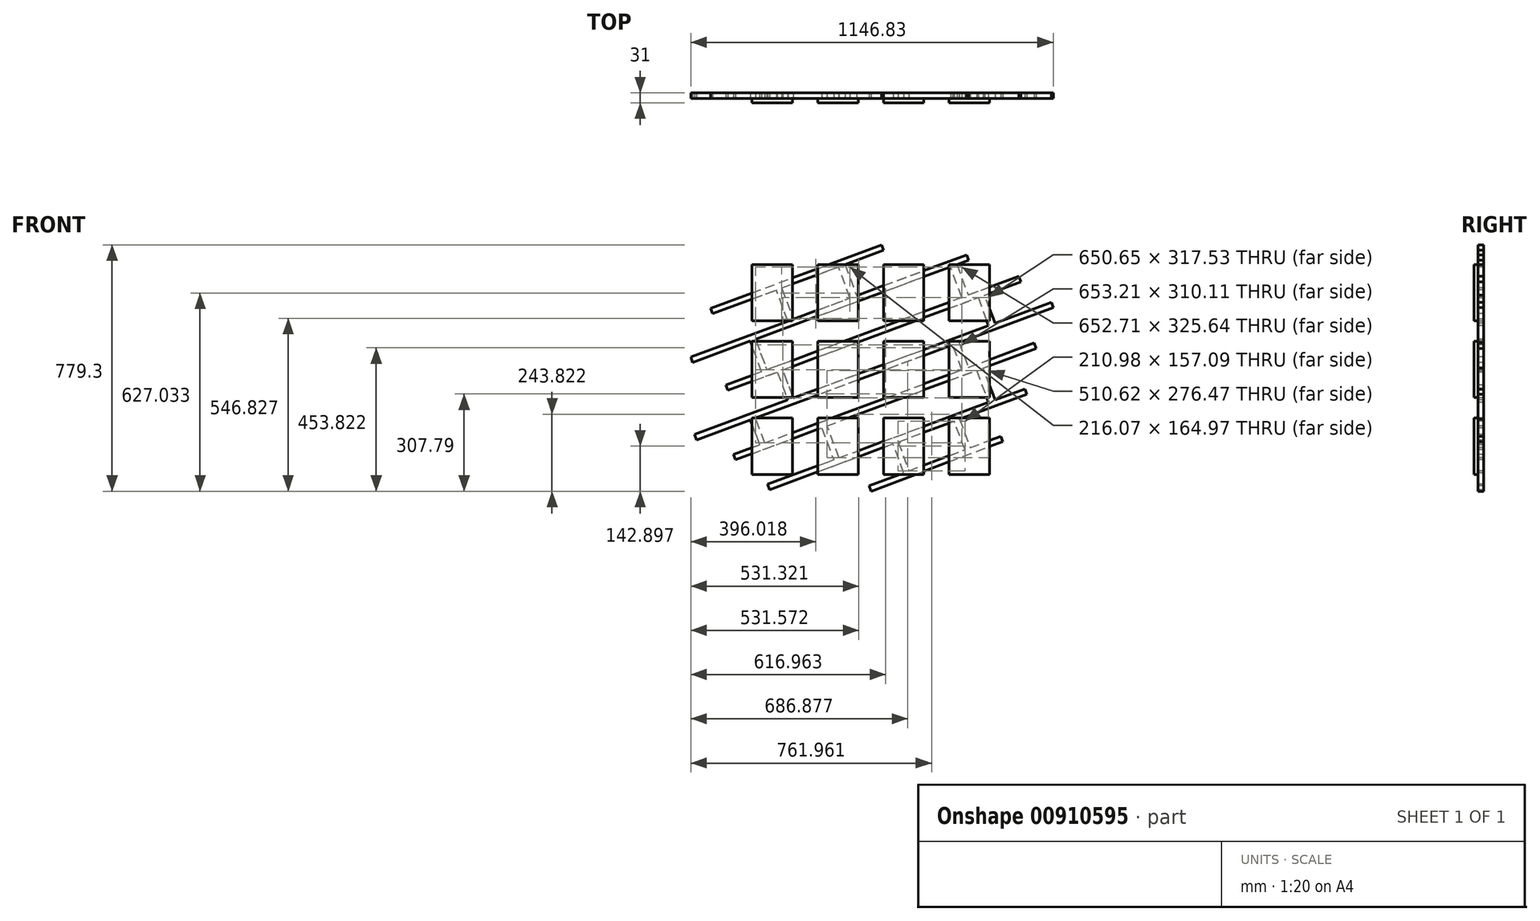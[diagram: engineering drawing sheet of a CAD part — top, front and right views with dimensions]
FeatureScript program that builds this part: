
annotation { "Feature Type Name" : "Feature", "Feature Type Description" : "" }
export const myFeature = defineFeature(function(context is Context, id is Id, definition is map)
    precondition{}
    {
        {
            var Q0;
            Q0=qCreatedBy(makeId("Front.planeOp"),FACE);
            var sketch = newSketch(context, id + "F0", { "sketchPlane" : qUnion([Q0])});
            skLineSegment(sketch, "E0.bottom", {"start": v(-52.91, 29.92) * mm, "end": v(75.09, 29.92) * mm});
            skLineSegment(sketch, "E0.top", {"start": v(-52.91, -148.08) * mm, "end": v(75.09, -148.08) * mm});
            skLineSegment(sketch, "E0.left", {"start": v(-52.91, 29.92) * mm, "end": v(-52.91, -148.08) * mm});
            skLineSegment(sketch, "E0.right", {"start": v(75.09, 29.92) * mm, "end": v(75.09, -148.08) * mm});
            skLineSegment(sketch, "E1.bottom", {"start": v(155.09, 29.92) * mm, "end": v(283.09, 29.92) * mm});
            skLineSegment(sketch, "E1.top", {"start": v(155.09, -148.08) * mm, "end": v(283.09, -148.08) * mm});
            skLineSegment(sketch, "E1.left", {"start": v(155.09, 29.92) * mm, "end": v(155.09, -148.08) * mm});
            skLineSegment(sketch, "E1.right", {"start": v(283.09, 29.92) * mm, "end": v(283.09, -148.08) * mm});
            skLineSegment(sketch, "E2.bottom", {"start": v(363.09, 29.92) * mm, "end": v(491.09, 29.92) * mm});
            skLineSegment(sketch, "E2.top", {"start": v(363.09, -148.08) * mm, "end": v(491.09, -148.08) * mm});
            skLineSegment(sketch, "E2.left", {"start": v(363.09, 29.92) * mm, "end": v(363.09, -148.08) * mm});
            skLineSegment(sketch, "E2.right", {"start": v(491.09, 29.92) * mm, "end": v(491.09, -148.08) * mm});
            skLineSegment(sketch, "E3.bottom", {"start": v(571.09, 29.92) * mm, "end": v(699.09, 29.92) * mm});
            skLineSegment(sketch, "E3.top", {"start": v(571.09, -148.08) * mm, "end": v(699.09, -148.08) * mm});
            skLineSegment(sketch, "E3.left", {"start": v(571.09, 29.92) * mm, "end": v(571.09, -148.08) * mm});
            skLineSegment(sketch, "E3.right", {"start": v(699.09, 29.92) * mm, "end": v(699.09, -148.08) * mm});
            skLineSegment(sketch, "E4.bottom", {"start": v(-52.91, -213.08) * mm, "end": v(75.09, -213.08) * mm});
            skLineSegment(sketch, "E4.top", {"start": v(-52.91, -391.08) * mm, "end": v(75.09, -391.08) * mm});
            skLineSegment(sketch, "E4.left", {"start": v(-52.91, -213.08) * mm, "end": v(-52.91, -391.08) * mm});
            skLineSegment(sketch, "E4.right", {"start": v(75.09, -213.08) * mm, "end": v(75.09, -391.08) * mm});
            skLineSegment(sketch, "E5.bottom", {"start": v(155.09, -213.08) * mm, "end": v(283.09, -213.08) * mm});
            skLineSegment(sketch, "E5.top", {"start": v(155.09, -391.08) * mm, "end": v(283.09, -391.08) * mm});
            skLineSegment(sketch, "E5.left", {"start": v(155.09, -213.08) * mm, "end": v(155.09, -391.08) * mm});
            skLineSegment(sketch, "E5.right", {"start": v(283.09, -213.08) * mm, "end": v(283.09, -391.08) * mm});
            skLineSegment(sketch, "E6.bottom", {"start": v(363.09, -213.08) * mm, "end": v(491.09, -213.08) * mm});
            skLineSegment(sketch, "E6.top", {"start": v(363.09, -391.08) * mm, "end": v(491.09, -391.08) * mm});
            skLineSegment(sketch, "E6.left", {"start": v(363.09, -213.08) * mm, "end": v(363.09, -391.08) * mm});
            skLineSegment(sketch, "E6.right", {"start": v(491.09, -213.08) * mm, "end": v(491.09, -391.08) * mm});
            skLineSegment(sketch, "E7.bottom", {"start": v(571.09, -213.08) * mm, "end": v(699.09, -213.08) * mm});
            skLineSegment(sketch, "E7.top", {"start": v(571.09, -391.08) * mm, "end": v(699.09, -391.08) * mm});
            skLineSegment(sketch, "E7.left", {"start": v(571.09, -213.08) * mm, "end": v(571.09, -391.08) * mm});
            skLineSegment(sketch, "E7.right", {"start": v(699.09, -213.08) * mm, "end": v(699.09, -391.08) * mm});
            skLineSegment(sketch, "E8.bottom", {"start": v(-52.91, -456.08) * mm, "end": v(75.09, -456.08) * mm});
            skLineSegment(sketch, "E8.top", {"start": v(-52.91, -634.08) * mm, "end": v(75.09, -634.08) * mm});
            skLineSegment(sketch, "E8.left", {"start": v(-52.91, -456.08) * mm, "end": v(-52.91, -634.08) * mm});
            skLineSegment(sketch, "E8.right", {"start": v(75.09, -456.08) * mm, "end": v(75.09, -634.08) * mm});
            skLineSegment(sketch, "E9.bottom", {"start": v(155.09, -456.08) * mm, "end": v(283.09, -456.08) * mm});
            skLineSegment(sketch, "E9.top", {"start": v(155.09, -634.08) * mm, "end": v(283.09, -634.08) * mm});
            skLineSegment(sketch, "E9.left", {"start": v(155.09, -456.08) * mm, "end": v(155.09, -634.08) * mm});
            skLineSegment(sketch, "E9.right", {"start": v(283.09, -456.08) * mm, "end": v(283.09, -634.08) * mm});
            skLineSegment(sketch, "E10.bottom", {"start": v(363.09, -456.08) * mm, "end": v(491.09, -456.08) * mm});
            skLineSegment(sketch, "E10.top", {"start": v(363.09, -634.08) * mm, "end": v(491.09, -634.08) * mm});
            skLineSegment(sketch, "E10.left", {"start": v(363.09, -456.08) * mm, "end": v(363.09, -634.08) * mm});
            skLineSegment(sketch, "E10.right", {"start": v(491.09, -456.08) * mm, "end": v(491.09, -634.08) * mm});
            skLineSegment(sketch, "E11.bottom", {"start": v(571.09, -456.08) * mm, "end": v(699.09, -456.08) * mm});
            skLineSegment(sketch, "E11.top", {"start": v(571.09, -634.08) * mm, "end": v(699.09, -634.08) * mm});
            skLineSegment(sketch, "E11.left", {"start": v(571.09, -456.08) * mm, "end": v(571.09, -634.08) * mm});
            skLineSegment(sketch, "E11.right", {"start": v(699.09, -456.08) * mm, "end": v(699.09, -634.08) * mm});
            skLineSegment(sketch, "E12", {"start": v(75.09, 29.92) * mm, "end": v(155.09, 29.92) * mm, "construction": true});
            skLineSegment(sketch, "E13", {"start": v(283.09, 29.92) * mm, "end": v(363.09, 29.92) * mm, "construction": true});
            skLineSegment(sketch, "E14", {"start": v(491.09, 29.92) * mm, "end": v(571.09, 29.92) * mm, "construction": true});
            skLineSegment(sketch, "E15", {"start": v(-52.91, -148.08) * mm, "end": v(-52.91, -213.08) * mm, "construction": true});
            skLineSegment(sketch, "E16", {"start": v(-52.91, -391.08) * mm, "end": v(-52.91, -456.08) * mm, "construction": true});
            skSolve(sketch);
        }
        {
            var Q0;
            Q0=makeQuery(id+"F0.imprint","IMPRINT",FACE,{"disambiguationData":[TD([[makeQuery(id+"F0.imprint","IMPRINT",EDGE,{"derivedFrom":sQuery(id+"F0.wireOp",EDGE,"E1.bottom")}),-1.0]])]});
            var Q1;
            Q1=makeQuery(id+"F0.imprint","IMPRINT",FACE,{"disambiguationData":[TD([[makeQuery(id+"F0.imprint","IMPRINT",EDGE,{"derivedFrom":sQuery(id+"F0.wireOp",EDGE,"E0.bottom")}),-1.0]])]});
            var Q2;
            Q2=makeQuery(id+"F0.imprint","IMPRINT",FACE,{"disambiguationData":[TD([[makeQuery(id+"F0.imprint","IMPRINT",EDGE,{"derivedFrom":sQuery(id+"F0.wireOp",EDGE,"E2.bottom")}),-1.0]])]});
            var Q3;
            Q3=makeQuery(id+"F0.imprint","IMPRINT",FACE,{"disambiguationData":[TD([[makeQuery(id+"F0.imprint","IMPRINT",EDGE,{"derivedFrom":sQuery(id+"F0.wireOp",EDGE,"E11.bottom")}),-1.0]])]});
            var Q4;
            Q4=makeQuery(id+"F0.imprint","IMPRINT",FACE,{"disambiguationData":[TD([[makeQuery(id+"F0.imprint","IMPRINT",EDGE,{"derivedFrom":sQuery(id+"F0.wireOp",EDGE,"E3.bottom")}),-1.0]])]});
            var Q5;
            Q5=makeQuery(id+"F0.imprint","IMPRINT",FACE,{"disambiguationData":[TD([[makeQuery(id+"F0.imprint","IMPRINT",EDGE,{"derivedFrom":sQuery(id+"F0.wireOp",EDGE,"E6.bottom")}),-1.0]])]});
            var Q6;
            Q6=makeQuery(id+"F0.imprint","IMPRINT",FACE,{"disambiguationData":[TD([[makeQuery(id+"F0.imprint","IMPRINT",EDGE,{"derivedFrom":sQuery(id+"F0.wireOp",EDGE,"E4.bottom")}),-1.0]])]});
            var Q7;
            Q7=makeQuery(id+"F0.imprint","IMPRINT",FACE,{"disambiguationData":[TD([[makeQuery(id+"F0.imprint","IMPRINT",EDGE,{"derivedFrom":sQuery(id+"F0.wireOp",EDGE,"E9.bottom")}),-1.0]])]});
            var Q8;
            Q8=makeQuery(id+"F0.imprint","IMPRINT",FACE,{"disambiguationData":[TD([[makeQuery(id+"F0.imprint","IMPRINT",EDGE,{"derivedFrom":sQuery(id+"F0.wireOp",EDGE,"E10.bottom")}),-1.0]])]});
            var Q9;
            Q9=makeQuery(id+"F0.imprint","IMPRINT",FACE,{"disambiguationData":[TD([[makeQuery(id+"F0.imprint","IMPRINT",EDGE,{"derivedFrom":sQuery(id+"F0.wireOp",EDGE,"E5.bottom")}),-1.0]])]});
            var Q10;
            Q10=makeQuery(id+"F0.imprint","IMPRINT",FACE,{"disambiguationData":[TD([[makeQuery(id+"F0.imprint","IMPRINT",EDGE,{"derivedFrom":sQuery(id+"F0.wireOp",EDGE,"E8.bottom")}),-1.0]])]});
            var Q11;
            Q11=makeQuery(id+"F0.imprint","IMPRINT",FACE,{"disambiguationData":[TD([[makeQuery(id+"F0.imprint","IMPRINT",EDGE,{"derivedFrom":sQuery(id+"F0.wireOp",EDGE,"E7.bottom")}),-1.0]])]});
            extrude(context, id + "F1", {"entities" : qUnion([Q0, Q1, Q2, Q3, Q4, Q5, Q6, Q7, Q8, Q9, Q10, Q11]), "depth" : 13 * mm, "offsetDistance" : 25 * mm});
        }
        {
            var Q0;
            Q0=qCreatedBy(makeId("Front.planeOp"),FACE);
            var sketch = newSketch(context, id + "F2", { "sketchPlane" : qUnion([Q0])});
            skLineSegment(sketch, "E17", {"start": v(-234.75, -508.14) * mm, "end": v(60.42, -398.74) * mm});
            skLineSegment(sketch, "E18", {"start": v(893.97, -89.8) * mm, "end": v(900.23, -106.68) * mm});
            skLineSegment(sketch, "E19", {"start": v(900.23, -106.68) * mm, "end": v(602.32, -217.1) * mm});
            skLineSegment(sketch, "E20", {"start": v(-129.54, -368.44) * mm, "end": v(27.6, -310.2) * mm});
            skLineSegment(sketch, "E21", {"start": v(798.05, -24.65) * mm, "end": v(791.8, -7.78) * mm});
            skLineSegment(sketch, "E22", {"start": v(791.8, -7.78) * mm, "end": v(631.54, -67.17) * mm});
            skLineSegment(sketch, "E23", {"start": v(-135.23, -351.36) * mm, "end": v(-129.54, -368.44) * mm});
            skLineSegment(sketch, "E24", {"start": v(-240.34, -279.92) * mm, "end": v(-57.93, -212.31) * mm});
            skLineSegment(sketch, "E25.0", {"start": v(-246.6, -263.04) * mm, "end": v(60.84, -149.1) * mm});
            skLineSegment(sketch, "E26", {"start": v(-111.19, -571.21) * mm, "end": v(-28.7, -540.64) * mm});
            skLineSegment(sketch, "E27", {"start": v(-3.7, -665.57) * mm, "end": v(205.55, -588) * mm});
            skLineSegment(sketch, "E28", {"start": v(317.55, -670.5) * mm, "end": v(427.52, -629.1) * mm});
            skLineSegment(sketch, "E29", {"start": v(-177.44, -125.49) * mm, "end": v(24.37, -50.7) * mm});
            skLineSegment(sketch, "E30.0", {"start": v(-183.7, -108.61) * mm, "end": v(357.46, 91.96) * mm});
            skLineSegment(sketch, "E31.0", {"start": v(-104.93, -588.1) * mm, "end": v(168.08, -486.9) * mm});
            skLineSegment(sketch, "E32.0", {"start": v(2.55, -682.44) * mm, "end": v(393.58, -537.52) * mm});
            skLineSegment(sketch, "E33.0", {"start": v(323.89, -687.34) * mm, "end": v(740.87, -530.42) * mm});
            skLineSegment(sketch, "E34", {"start": v(-234.75, -508.14) * mm, "end": v(-228.5, -525.02) * mm});
            skLineSegment(sketch, "E35", {"start": v(-246.6, -263.04) * mm, "end": v(-240.34, -279.92) * mm});
            skLineSegment(sketch, "E36", {"start": v(-111.19, -571.21) * mm, "end": v(-104.93, -588.1) * mm});
            skLineSegment(sketch, "E37", {"start": v(-3.7, -665.57) * mm, "end": v(2.55, -682.44) * mm});
            skLineSegment(sketch, "E38", {"start": v(317.55, -670.5) * mm, "end": v(323.89, -687.34) * mm});
            skLineSegment(sketch, "E39", {"start": v(740.87, -530.42) * mm, "end": v(734.53, -513.58) * mm});
            skLineSegment(sketch, "E40", {"start": v(817.2, -380.51) * mm, "end": v(810.94, -363.64) * mm});
            skLineSegment(sketch, "E41", {"start": v(846.5, -235.46) * mm, "end": v(840.25, -218.58) * mm});
            skLineSegment(sketch, "E42", {"start": v(-177.44, -125.49) * mm, "end": v(-183.7, -108.61) * mm});
            skLineSegment(sketch, "E43", {"start": v(363.72, 75.08) * mm, "end": v(357.46, 91.96) * mm});
            skLineSegment(sketch, "E44", {"start": v(626.24, 60.46) * mm, "end": v(632.5, 43.58) * mm});
            skLineSegment(sketch, "E45", {"start": v(60.84, -149.1) * mm, "end": v(24.37, -50.7) * mm});
            skLineSegment(sketch, "E46", {"start": v(41.38, -44.39) * mm, "end": v(77.85, -142.8) * mm});
            skLineSegment(sketch, "E47", {"start": v(241.8, 29.9) * mm, "end": v(278.27, -68.51) * mm});
            skLineSegment(sketch, "E48", {"start": v(257.45, -76.23) * mm, "end": v(220.98, 22.18) * mm});
            skLineSegment(sketch, "E49", {"start": v(595.56, 29.9) * mm, "end": v(631.54, -67.17) * mm});
            skLineSegment(sketch, "E50", {"start": v(611.08, -74.75) * mm, "end": v(575.1, 22.3) * mm});
            skLineSegment(sketch, "E51", {"start": v(-41.64, -206.27) * mm, "end": v(-5.66, -303.34) * mm});
            skLineSegment(sketch, "E52", {"start": v(-22.55, -309.6) * mm, "end": v(-57.93, -212.31) * mm});
            skLineSegment(sketch, "E53", {"start": v(716.1, -155.73) * mm, "end": v(683.27, -67.17) * mm});
            skLineSegment(sketch, "E54", {"start": v(662.87, -74.75) * mm, "end": v(695.69, -163.3) * mm});
            skLineSegment(sketch, "E55", {"start": v(77.85, -392.28) * mm, "end": v(45.04, -303.74) * mm});
            skLineSegment(sketch, "E56", {"start": v(27.6, -310.2) * mm, "end": v(60.42, -398.74) * mm});
            skLineSegment(sketch, "E57", {"start": v(602.32, -217.1) * mm, "end": v(631.54, -295.94) * mm});
            skLineSegment(sketch, "E58", {"start": v(611.58, -303.34) * mm, "end": v(582.36, -224.5) * mm});
            skLineSegment(sketch, "E59", {"start": v(-57.93, -461.8) * mm, "end": v(-28.7, -540.64) * mm});
            skLineSegment(sketch, "E60", {"start": v(-12.41, -534.6) * mm, "end": v(-41.64, -455.76) * mm});
            skLineSegment(sketch, "E61", {"start": v(716.1, -398.79) * mm, "end": v(678.62, -297.68) * mm});
            skLineSegment(sketch, "E62", {"start": v(658.12, -305.28) * mm, "end": v(695.59, -406.39) * mm});
            skLineSegment(sketch, "E63", {"start": v(168.08, -486.9) * mm, "end": v(205.55, -588) * mm});
            skLineSegment(sketch, "E64", {"start": v(222.44, -581.75) * mm, "end": v(184.96, -480.65) * mm});
            skLineSegment(sketch, "E65", {"start": v(427.52, -629.1) * mm, "end": v(393.58, -537.52) * mm});
            skLineSegment(sketch, "E66", {"start": v(409.87, -531.48) * mm, "end": v(443.79, -622.99) * mm});
            skLineSegment(sketch, "E67", {"start": v(604.14, -459.48) * mm, "end": v(638.15, -549.85) * mm});
            skLineSegment(sketch, "E68", {"start": v(620.85, -556.36) * mm, "end": v(586.8, -465.9) * mm});
            skLineSegment(sketch, "E69.trimOffspring", {"start": v(41.38, -44.39) * mm, "end": v(220.98, 22.18) * mm});
            skLineSegment(sketch, "E70.trimOffspring", {"start": v(241.8, 29.9) * mm, "end": v(363.72, 75.08) * mm});
            skLineSegment(sketch, "E71.trimOffspring", {"start": v(77.85, -142.8) * mm, "end": v(257.45, -76.23) * mm});
            skLineSegment(sketch, "E72.trimOffspring", {"start": v(278.27, -68.51) * mm, "end": v(626.24, 60.46) * mm});
            skLineSegment(sketch, "E73.trimOffspring", {"start": v(-22.55, -309.6) * mm, "end": v(-135.23, -351.36) * mm});
            skLineSegment(sketch, "E74.trimOffspring", {"start": v(-41.64, -206.27) * mm, "end": v(575.1, 22.3) * mm});
            skLineSegment(sketch, "E75.trimOffspring", {"start": v(77.85, -392.28) * mm, "end": v(695.69, -163.3) * mm});
            skPoint(sketch, "E76.orphan", {"position": v(60.84, -399.88) * mm});
            skPoint(sketch, "E77.orphan", {"position": v(27.38, -309.6) * mm});
            skLineSegment(sketch, "E78.trimOffspring", {"start": v(45.04, -303.74) * mm, "end": v(662.87, -74.75) * mm});
            skPoint(sketch, "E79.orphan", {"position": v(44.89, -303.34) * mm});
            skLineSegment(sketch, "E80.trimOffspring", {"start": v(-12.41, -534.6) * mm, "end": v(611.58, -303.34) * mm});
            skLineSegment(sketch, "E81.trimOffspring", {"start": v(-57.93, -461.8) * mm, "end": v(-228.5, -525.02) * mm});
            skLineSegment(sketch, "E82.trimOffspring", {"start": v(184.96, -480.65) * mm, "end": v(658.12, -305.28) * mm});
            skLineSegment(sketch, "E83.trimOffspring", {"start": v(222.44, -581.75) * mm, "end": v(695.59, -406.39) * mm});
            skLineSegment(sketch, "E84.trimOffspring", {"start": v(409.87, -531.48) * mm, "end": v(586.8, -465.9) * mm});
            skLineSegment(sketch, "E85.trimOffspring", {"start": v(443.79, -622.99) * mm, "end": v(620.85, -556.36) * mm});
            skLineSegment(sketch, "E86.trimOffspring", {"start": v(638.15, -549.85) * mm, "end": v(734.53, -513.58) * mm});
            skLineSegment(sketch, "E87.trimOffspring", {"start": v(604.14, -459.48) * mm, "end": v(817.2, -380.51) * mm});
            skLineSegment(sketch, "E88.trimOffspring", {"start": v(716.1, -398.79) * mm, "end": v(810.94, -363.64) * mm});
            skPoint(sketch, "E89.orphan", {"position": v(695.69, -406.66) * mm});
            skLineSegment(sketch, "E90.trimOffspring", {"start": v(678.62, -297.68) * mm, "end": v(846.5, -235.46) * mm});
            skLineSegment(sketch, "E91.trimOffspring", {"start": v(631.54, -295.94) * mm, "end": v(840.25, -218.58) * mm});
            skLineSegment(sketch, "E92.trimOffspring", {"start": v(582.36, -224.5) * mm, "end": v(-41.64, -455.76) * mm});
            skLineSegment(sketch, "E93.trimOffspring", {"start": v(716.1, -155.73) * mm, "end": v(893.97, -89.8) * mm});
            skLineSegment(sketch, "E94.trimOffspring", {"start": v(611.08, -74.75) * mm, "end": v(-5.66, -303.34) * mm});
            skLineSegment(sketch, "E95.trimOffspring", {"start": v(683.28, -67.19) * mm, "end": v(798.05, -24.65) * mm});
            skLineSegment(sketch, "E96.trimOffspring", {"start": v(595.56, 29.9) * mm, "end": v(632.5, 43.58) * mm});
            skSolve(sketch);
        }
        {
            var Q0;
            Q0=makeQuery(id+"F2.imprint","IMPRINT",FACE,{"disambiguationData":[TD([[makeQuery(id+"F2.imprint","IMPRINT",EDGE,{"derivedFrom":sQuery(id+"F2.wireOp",EDGE,"E30.0")}),-1.0]])]});
            var Q1;
            Q1=makeQuery(id+"F2.imprint","IMPRINT",FACE,{"disambiguationData":[TD([[makeQuery(id+"F2.imprint","IMPRINT",EDGE,{"derivedFrom":sQuery(id+"F2.wireOp",EDGE,"E45")}),-1.0]])]});
            var Q2;
            Q2=makeQuery(id+"F2.imprint","IMPRINT",FACE,{"disambiguationData":[TD([[makeQuery(id+"F2.imprint","IMPRINT",EDGE,{"derivedFrom":sQuery(id+"F2.wireOp",EDGE,"E47")}),-1.0]])]});
            var Q3;
            {var subQ2=sQuery(id+"F2.wireOp",EDGE,"E35");Q3=makeQuery(id+"F2.imprint","IMPRINT",FACE,{"disambiguationData":[TD([[makeQuery(id+"F2.imprint","IMPRINT",EDGE,{"derivedFrom":subQ2}),1.0]])]});}
            var Q4;
            Q4=makeQuery(id+"F2.imprint","IMPRINT",FACE,{"disambiguationData":[TD([[makeQuery(id+"F2.imprint","IMPRINT",EDGE,{"derivedFrom":sQuery(id+"F2.wireOp",EDGE,"fgwRCP9X-oQwL-n9JF-0mIb-ahIyvdE6cdXr")}),-1.0]])]});
            var Q5;
            Q5=makeQuery(id+"F2.imprint","IMPRINT",FACE,{"disambiguationData":[TD([[makeQuery(id+"F2.imprint","IMPRINT",EDGE,{"derivedFrom":sQuery(id+"F2.wireOp",EDGE,"E49")}),-1.0]])]});
            var Q6;
            {var subQ10=sQuery(id+"F2.wireOp",EDGE,"E21");Q6=makeQuery(id+"F2.imprint","IMPRINT",FACE,{"disambiguationData":[TD([[makeQuery(id+"F2.imprint","IMPRINT",EDGE,{"derivedFrom":subQ10}),1.0]])]});}
            var Q7;
            Q7=makeQuery(id+"F2.imprint","IMPRINT",FACE,{"disambiguationData":[TD([[makeQuery(id+"F2.imprint","IMPRINT",EDGE,{"derivedFrom":sQuery(id+"F2.wireOp",EDGE,"E53")}),1.0]])]});
            var Q8;
            {var subQ3=sQuery(id+"F2.wireOp",EDGE,"E56");var subQ5=sQuery(id+"F2.wireOp",EDGE,"E20");var subQ6=makeQuery(id+"F2.imprint","INTERSECT",VERTEX,{"derivedFrom":[subQ5,subQ3]});Q8=makeQuery(id+"F2.imprint","IMPRINT",FACE,{"disambiguationData":[TD([[makeQuery(id+"F2.imprint","IMPRINT",EDGE,{"disambiguationData":[TD([[subQ6,-1.0]])],"derivedFrom":subQ5}),-1.0]])]});}
            var Q9;
            {var subQ2=sQuery(id+"F2.wireOp",EDGE,"E18");Q9=makeQuery(id+"F2.imprint","IMPRINT",FACE,{"disambiguationData":[TD([[makeQuery(id+"F2.imprint","IMPRINT",EDGE,{"derivedFrom":subQ2}),-1.0]])]});}
            var Q10;
            {var subQ5=sQuery(id+"F2.wireOp",EDGE,"E36");Q10=makeQuery(id+"F2.imprint","IMPRINT",FACE,{"disambiguationData":[TD([[makeQuery(id+"F2.imprint","IMPRINT",EDGE,{"derivedFrom":subQ5}),1.0]])]});}
            var Q11;
            Q11=makeQuery(id+"F2.imprint","IMPRINT",FACE,{"disambiguationData":[TD([[makeQuery(id+"F2.imprint","IMPRINT",EDGE,{"derivedFrom":sQuery(id+"F2.wireOp",EDGE,"E59")}),1.0]])]});
            var Q12;
            Q12=makeQuery(id+"F2.imprint","IMPRINT",FACE,{"disambiguationData":[TD([[makeQuery(id+"F2.imprint","IMPRINT",EDGE,{"derivedFrom":sQuery(id+"F2.wireOp",EDGE,"E63")}),1.0]])]});
            var Q13;
            {var subQ0=sQuery(id+"F2.wireOp",EDGE,"E61");Q13=makeQuery(id+"F2.imprint","IMPRINT",FACE,{"disambiguationData":[TD([[makeQuery(id+"F2.imprint","IMPRINT",EDGE,{"derivedFrom":subQ0}),1.0]])]});}
            var Q14;
            {var subQ6=sQuery(id+"F2.wireOp",EDGE,"E37");Q14=makeQuery(id+"F2.imprint","IMPRINT",FACE,{"disambiguationData":[TD([[makeQuery(id+"F2.imprint","IMPRINT",EDGE,{"derivedFrom":subQ6}),1.0]])]});}
            var Q15;
            Q15=makeQuery(id+"F2.imprint","IMPRINT",FACE,{"disambiguationData":[TD([[makeQuery(id+"F2.imprint","IMPRINT",EDGE,{"derivedFrom":sQuery(id+"F2.wireOp",EDGE,"E65")}),-1.0]])]});
            var Q16;
            Q16=makeQuery(id+"F2.imprint","IMPRINT",FACE,{"disambiguationData":[TD([[makeQuery(id+"F2.imprint","IMPRINT",EDGE,{"derivedFrom":sQuery(id+"F2.wireOp",EDGE,"E67")}),-1.0]])]});
            var Q17;
            Q17=makeQuery(id+"F2.imprint","IMPRINT",FACE,{"disambiguationData":[TD([[makeQuery(id+"F2.imprint","IMPRINT",EDGE,{"derivedFrom":sQuery(id+"F2.wireOp",EDGE,"E33.0")}),1.0]])]});
            var Q18;
            Q18=makeQuery(id+"F2.imprint","IMPRINT",FACE,{"disambiguationData":[TD([[makeQuery(id+"F2.imprint","IMPRINT",EDGE,{"derivedFrom":sQuery(id+"F2.wireOp",EDGE,"E57")}),-1.0]])]});
            extrude(context, id + "F3", {"entities" : qUnion([Q0, Q1, Q2, Q3, Q4, Q5, Q6, Q7, Q8, Q9, Q10, Q11, Q12, Q13, Q14, Q15, Q16, Q17, Q18]), "oppositeDirection" : true, "depth" : 18 * mm, "offsetDistance" : 25 * mm});
        }
    });
